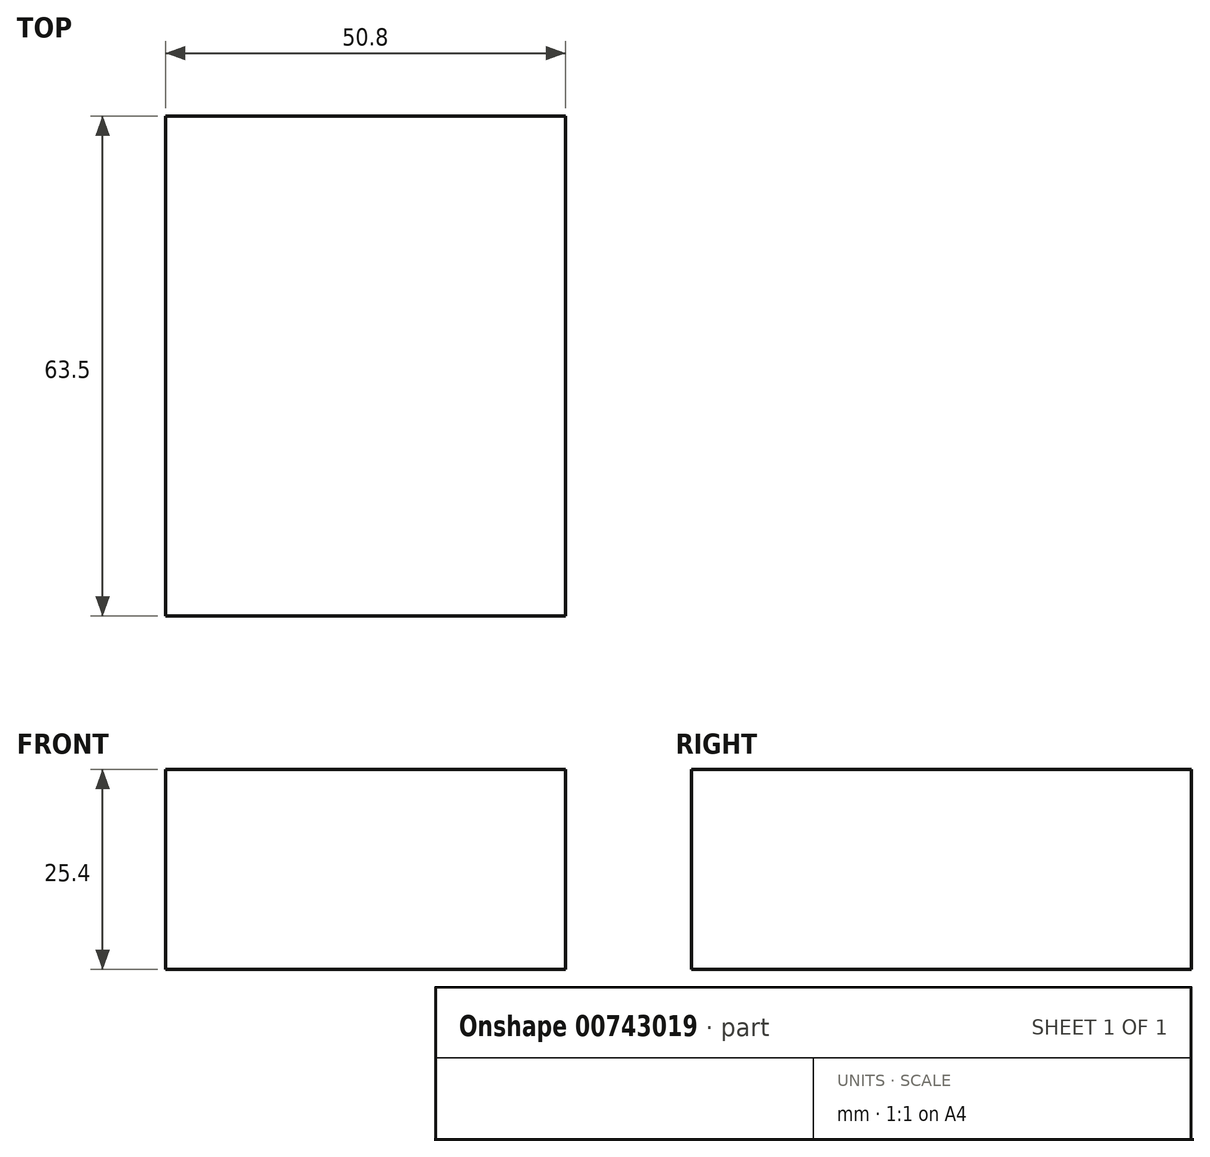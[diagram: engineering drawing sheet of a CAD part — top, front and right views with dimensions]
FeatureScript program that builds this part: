
annotation { "Feature Type Name" : "Feature", "Feature Type Description" : "" }
export const myFeature = defineFeature(function(context is Context, id is Id, definition is map)
    precondition{}
    {
        {
            var Q0;
            Q0=qCreatedBy(makeId("Top.planeOp"),FACE);
            var sketch = newSketch(context, id + "F0", { "sketchPlane" : qUnion([Q0])});
            skLineSegment(sketch, "E0.bottom", {"start": v(-25.4, 31.75) * mm, "end": v(25.4, 31.75) * mm});
            skLineSegment(sketch, "E0.top", {"start": v(-25.4, -31.75) * mm, "end": v(25.4, -31.75) * mm});
            skLineSegment(sketch, "E0.left", {"start": v(-25.4, 31.75) * mm, "end": v(-25.4, -31.75) * mm});
            skLineSegment(sketch, "E0.right", {"start": v(25.4, 31.75) * mm, "end": v(25.4, -31.75) * mm});
            skPoint(sketch, "E0.middle", {"position": v(0, 0) * mm});
            skSolve(sketch);
        }
        {
            var Q0;
            Q0=makeQuery(id+"F0.imprint","IMPRINT",FACE,{"disambiguationData":[TD([[makeQuery(id+"F0.imprint","IMPRINT",EDGE,{"derivedFrom":sQuery(id+"F0.wireOp",EDGE,"E0.bottom")}),-1.0]])]});
            extrude(context, id + "F1", {"entities" : qUnion([Q0]), "depth" : 25.4 * mm, "offsetDistance" : 25.4 * mm});
        }
    });
